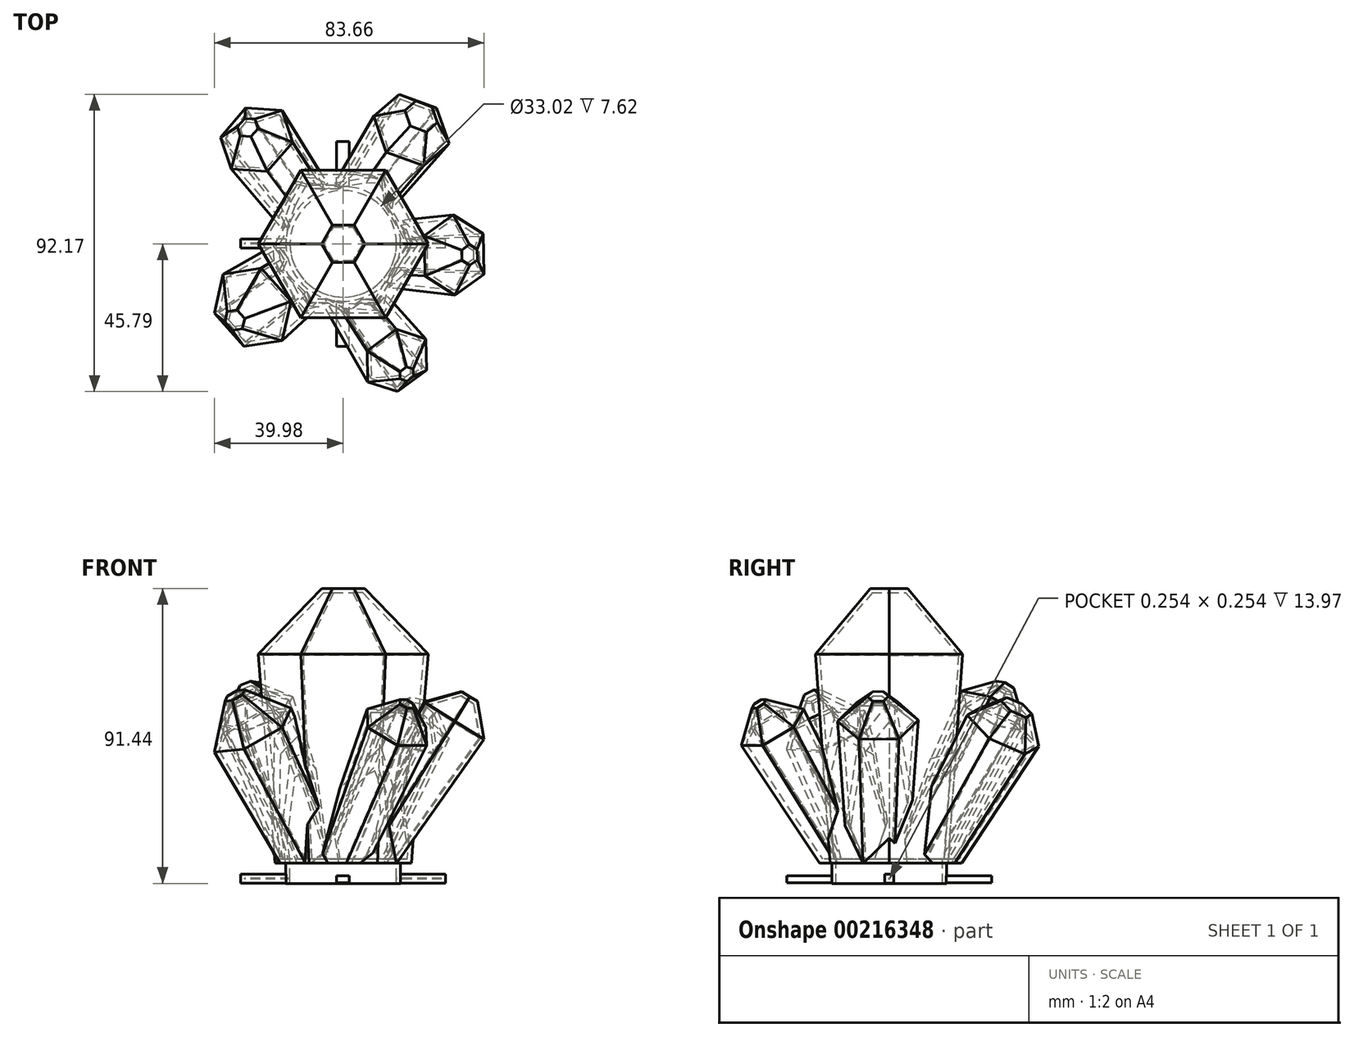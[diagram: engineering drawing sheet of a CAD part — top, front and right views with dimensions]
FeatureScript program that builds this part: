
annotation { "Feature Type Name" : "Feature", "Feature Type Description" : "" }
export const myFeature = defineFeature(function(context is Context, id is Id, definition is map)
    precondition{}
    {
        {
            var Q0;
            Q0=qCreatedBy(makeId("Top.planeOp"),FACE);
            cPlane(context, id + "F0", {"entities" : qUnion([Q0]), "cplaneType" : CPlaneType.OFFSET, "offset" : 35.56 * mm, "oppositeDirection" : true, "width" : 152.4 * mm, "height" : 152.4 * mm});
        }
        {
            var Q0;
            Q0=qCreatedBy(makeId("Top.planeOp"),FACE);
            var sketch = newSketch(context, id + "F1", { "sketchPlane" : qUnion([Q0])});
            skCircle(sketch, "E0.cCircle", {"center": v(0, 0) * mm, "radius": 38.1 * mm, "construction": true});
            skLineSegment(sketch, "E0.0", {"start": v(-12.38, 38.1) * mm, "end": v(12.38, 38.1) * mm});
            skLineSegment(sketch, "E0.1", {"start": v(12.38, 38.1) * mm, "end": v(32.4, 23.55) * mm});
            skLineSegment(sketch, "E0.2", {"start": v(32.4, 23.55) * mm, "end": v(40.06, 0) * mm});
            skLineSegment(sketch, "E0.3", {"start": v(40.06, 0) * mm, "end": v(32.4, -23.55) * mm});
            skLineSegment(sketch, "E0.4", {"start": v(32.4, -23.55) * mm, "end": v(12.38, -38.1) * mm});
            skLineSegment(sketch, "E0.5", {"start": v(12.38, -38.1) * mm, "end": v(-12.38, -38.1) * mm});
            skLineSegment(sketch, "E0.6", {"start": v(-12.38, -38.1) * mm, "end": v(-32.4, -23.55) * mm});
            skLineSegment(sketch, "E0.7", {"start": v(-32.4, -23.55) * mm, "end": v(-40.06, 0) * mm});
            skLineSegment(sketch, "E0.8", {"start": v(-40.06, 0) * mm, "end": v(-32.4, 23.55) * mm});
            skLineSegment(sketch, "E0.9", {"start": v(-32.4, 23.55) * mm, "end": v(-12.38, 38.1) * mm});
            skPoint(sketch, "E0.0.midPoint", {"position": v(0, 38.1) * mm});
            skSolve(sketch);
        }
        {
            var Q0;
            Q0=qCreatedBy(id+"F0.planeOp",FACE);
            var sketch = newSketch(context, id + "F2", { "sketchPlane" : qUnion([Q0])});
            skCircle(sketch, "E1.cCircle", {"center": v(0, 0) * mm, "radius": 19.05 * mm, "construction": true});
            skLineSegment(sketch, "E1.0", {"start": v(-6.19, 19.05) * mm, "end": v(6.19, 19.05) * mm});
            skLineSegment(sketch, "E1.1", {"start": v(6.19, 19.05) * mm, "end": v(16.2, 11.77) * mm});
            skLineSegment(sketch, "E1.2", {"start": v(16.2, 11.77) * mm, "end": v(20.03, 0) * mm});
            skLineSegment(sketch, "E1.3", {"start": v(20.03, 0) * mm, "end": v(16.2, -11.77) * mm});
            skLineSegment(sketch, "E1.4", {"start": v(16.2, -11.77) * mm, "end": v(6.19, -19.05) * mm});
            skLineSegment(sketch, "E1.5", {"start": v(6.19, -19.05) * mm, "end": v(-6.19, -19.05) * mm});
            skLineSegment(sketch, "E1.6", {"start": v(-6.19, -19.05) * mm, "end": v(-16.2, -11.77) * mm});
            skLineSegment(sketch, "E1.7", {"start": v(-16.2, -11.77) * mm, "end": v(-20.03, 0) * mm});
            skLineSegment(sketch, "E1.8", {"start": v(-20.03, 0) * mm, "end": v(-16.2, 11.77) * mm});
            skLineSegment(sketch, "E1.9", {"start": v(-16.2, 11.77) * mm, "end": v(-6.19, 19.05) * mm});
            skPoint(sketch, "E1.0.midPoint", {"position": v(0, 19.05) * mm});
            skSolve(sketch);
        }
        {
            var Q0;
            Q0=sQuery(id+"F1.wireOp",VERTEX,"E0.8.start");
            var Q1;
            Q1=sQuery(id+"F2.wireOp",VERTEX,"E1.2.start");
            var Q2;
            Q2=sQuery(id+"F2.wireOp",VERTEX,"E1.4.start");
            cPlane(context, id + "F3", {"entities" : qUnion([Q0, Q1, Q2]), "cplaneType" : CPlaneType.THREE_POINT, "offset" : 25.4 * mm, "width" : 152.4 * mm, "height" : 152.4 * mm});
        }
        {
            var Q0;
            Q0=sQuery(id+"F1.wireOp",VERTEX,"E0.6.start");
            var Q1;
            Q1=sQuery(id+"F2.wireOp",VERTEX,"E1.9.end");
            var Q2;
            Q2=sQuery(id+"F2.wireOp",VERTEX,"E1.3.start");
            cPlane(context, id + "F4", {"entities" : qUnion([Q0, Q1, Q2]), "cplaneType" : CPlaneType.THREE_POINT, "offset" : 25.4 * mm, "width" : 152.4 * mm, "height" : 152.4 * mm});
        }
        {
            var Q0;
            Q0=sQuery(id+"F1.wireOp",VERTEX,"E0.4.start");
            var Q1;
            Q1=sQuery(id+"F2.wireOp",VERTEX,"E1.9.end");
            var Q2;
            Q2=sQuery(id+"F2.wireOp",VERTEX,"E1.8.end");
            cPlane(context, id + "F5", {"entities" : qUnion([Q0, Q1, Q2]), "cplaneType" : CPlaneType.THREE_POINT, "offset" : 25.4 * mm, "width" : 152.4 * mm, "height" : 152.4 * mm});
        }
        {
            var Q0;
            Q0=sQuery(id+"F1.wireOp",VERTEX,"E0.2.start");
            var Q1;
            Q1=sQuery(id+"F2.wireOp",VERTEX,"E1.8.start");
            var Q2;
            Q2=sQuery(id+"F2.wireOp",VERTEX,"E1.6.start");
            cPlane(context, id + "F6", {"entities" : qUnion([Q0, Q1, Q2]), "cplaneType" : CPlaneType.THREE_POINT, "offset" : 25.4 * mm, "width" : 152.4 * mm, "height" : 152.4 * mm});
        }
        {
            var Q0;
            Q0=sQuery(id+"F1.wireOp",VERTEX,"E0.9.end");
            var Q1;
            Q1=sQuery(id+"F2.wireOp",VERTEX,"E1.6.start");
            var Q2;
            Q2=sQuery(id+"F2.wireOp",VERTEX,"E1.3.start");
            cPlane(context, id + "F7", {"entities" : qUnion([Q0, Q1, Q2]), "cplaneType" : CPlaneType.THREE_POINT, "offset" : 25.4 * mm, "width" : 152.4 * mm, "height" : 152.4 * mm});
        }
        {
            var Q0;
            Q0=qCreatedBy(id+"F0.planeOp",FACE);
            var sketch = newSketch(context, id + "F8", { "sketchPlane" : qUnion([Q0])});
            skCircle(sketch, "E2.cCircle", {"center": v(0, 0) * mm, "radius": 17.14 * mm, "construction": true});
            skLineSegment(sketch, "E2.0", {"start": v(-9.9, 17.14) * mm, "end": v(9.9, 17.14) * mm});
            skLineSegment(sketch, "E2.1", {"start": v(9.9, 17.15) * mm, "end": v(19.8, 0) * mm});
            skLineSegment(sketch, "E2.2", {"start": v(19.8, 0) * mm, "end": v(9.9, -17.14) * mm});
            skLineSegment(sketch, "E2.3", {"start": v(9.9, -17.15) * mm, "end": v(-9.9, -17.15) * mm});
            skLineSegment(sketch, "E2.4", {"start": v(-9.9, -17.15) * mm, "end": v(-19.8, 0) * mm});
            skLineSegment(sketch, "E2.5", {"start": v(-19.8, 0) * mm, "end": v(-9.9, 17.15) * mm});
            skPoint(sketch, "E2.0.midPoint", {"position": v(0, 17.14) * mm});
            skSolve(sketch);
        }
        {
            var Q0;
            Q0 = qSketchRegion(id + "F8", true);
            extrude(context, id + "F9", {"entities" : qUnion([Q0]), "depth" : 81.28 * mm, "hasDraft" : true, "draftAngle" : 4 * degree});
        }
        {
            var Q0;
            Q0=makeQuery(id+"F9.opExtrude","CAP_FACE",FACE,{"disambiguationData":[OSD([sQuery(id+"F8.wireOp",EDGE,"E2.0"),sQuery(id+"F8.wireOp",EDGE,"E2.1"),sQuery(id+"F8.wireOp",EDGE,"E2.2"),sQuery(id+"F8.wireOp",EDGE,"E2.3"),sQuery(id+"F8.wireOp",EDGE,"E2.4"),sQuery(id+"F8.wireOp",EDGE,"E2.5")])],"isStart":false});
            var sketch = newSketch(context, id + "F10", { "sketchPlane" : qUnion([Q0])});
            skCircle(sketch, "E3.cCircle", {"center": v(0, 0) * mm, "radius": 22.83 * mm, "construction": true});
            skLineSegment(sketch, "E3.0", {"start": v(-13.18, 22.83) * mm, "end": v(13.18, 22.83) * mm});
            skLineSegment(sketch, "E3.1", {"start": v(13.18, 22.83) * mm, "end": v(26.36, 0) * mm});
            skLineSegment(sketch, "E3.2", {"start": v(26.36, 0) * mm, "end": v(13.18, -22.83) * mm});
            skLineSegment(sketch, "E3.3", {"start": v(13.18, -22.83) * mm, "end": v(-13.18, -22.83) * mm});
            skLineSegment(sketch, "E3.4", {"start": v(-13.18, -22.83) * mm, "end": v(-26.36, 0) * mm});
            skLineSegment(sketch, "E3.5", {"start": v(-26.36, 0) * mm, "end": v(-13.18, 22.83) * mm});
            skPoint(sketch, "E3.0.midPoint", {"position": v(0, 22.83) * mm});
            skSolve(sketch);
        }
        {
            var Q0;
            Q0 = qSketchRegion(id + "F10", true);
            extrude(context, id + "F11", {"entities" : qUnion([Q0]), "operationType" : NewBodyOperationType.ADD, "depth" : 20.32 * mm, "hasDraft" : true, "draftAngle" : 40 * degree, "draftPullDirection" : true});
        }
        {
            var Q0;
            Q0=qCreatedBy(id+"F3.planeOp",FACE);
            var sketch = newSketch(context, id + "F12", { "sketchPlane" : qUnion([Q0])});
            skCircle(sketch, "E4.cCircle", {"center": v(15.7, -3.44) * mm, "radius": 7.62 * mm, "construction": true});
            skLineSegment(sketch, "E4.0", {"start": v(7.97, 0.77) * mm, "end": v(15.47, 5.36) * mm});
            skLineSegment(sketch, "E4.1", {"start": v(15.47, 5.36) * mm, "end": v(23.2, 1.15) * mm});
            skLineSegment(sketch, "E4.2", {"start": v(23.2, 1.15) * mm, "end": v(23.43, -7.64) * mm});
            skLineSegment(sketch, "E4.3", {"start": v(23.43, -7.64) * mm, "end": v(15.92, -12.23) * mm});
            skLineSegment(sketch, "E4.4", {"start": v(15.92, -12.23) * mm, "end": v(8.2, -8.03) * mm});
            skLineSegment(sketch, "E4.5", {"start": v(8.2, -8.03) * mm, "end": v(7.97, 0.77) * mm});
            skPoint(sketch, "E4.0.midPoint", {"position": v(11.72, 3.06) * mm});
            skSolve(sketch);
        }
        {
            var Q0;
            Q0 = qSketchRegion(id + "F12", true);
            extrude(context, id + "F13", {"entities" : qUnion([Q0]), "operationType" : NewBodyOperationType.ADD, "depth" : 60.96 * mm, "hasDraft" : true, "draftAngle" : 3 * degree});
        }
        {
            var Q0;
            Q0=makeQuery(id+"F13.opExtrude","CAP_FACE",FACE,{"disambiguationData":[OSD([sQuery(id+"F12.wireOp",EDGE,"E4.0"),sQuery(id+"F12.wireOp",EDGE,"E4.1"),sQuery(id+"F12.wireOp",EDGE,"E4.2"),sQuery(id+"F12.wireOp",EDGE,"E4.3"),sQuery(id+"F12.wireOp",EDGE,"E4.4"),sQuery(id+"F12.wireOp",EDGE,"E4.5")])],"isStart":false});
            var sketch = newSketch(context, id + "F14", { "sketchPlane" : qUnion([Q0])});
            skLineSegment(sketch, "E5", {"start": v(4.73, 2.53) * mm, "end": v(26.67, -9.4) * mm, "construction": true});
            skPoint(sketch, "E6", {"position": v(15.7, -3.44) * mm});
            skCircle(sketch, "E7.cCircle", {"center": v(15.7, -3.44) * mm, "radius": 10.81 * mm, "construction": true});
            skLineSegment(sketch, "E7.0", {"start": v(15.38, 9.05) * mm, "end": v(26.35, 3.08) * mm});
            skLineSegment(sketch, "E7.1", {"start": v(26.35, 3.08) * mm, "end": v(26.67, -9.4) * mm});
            skLineSegment(sketch, "E7.2", {"start": v(26.67, -9.4) * mm, "end": v(16.01, -15.92) * mm});
            skLineSegment(sketch, "E7.3", {"start": v(16.01, -15.92) * mm, "end": v(5.04, -9.95) * mm});
            skLineSegment(sketch, "E7.4", {"start": v(5.04, -9.95) * mm, "end": v(4.73, 2.53) * mm});
            skLineSegment(sketch, "E7.5", {"start": v(4.73, 2.53) * mm, "end": v(15.38, 9.05) * mm});
            skPoint(sketch, "E7.0.midPoint", {"position": v(20.86, 6.06) * mm});
            skSolve(sketch);
        }
        {
            var Q0;
            Q0 = qSketchRegion(id + "F14", true);
            extrude(context, id + "F15", {"entities" : qUnion([Q0]), "operationType" : NewBodyOperationType.ADD, "depth" : 8.9 * mm, "hasDraft" : true, "draftAngle" : 42 * degree, "draftPullDirection" : true});
        }
        {
            var Q0;
            Q0=qCreatedBy(id+"F4.planeOp",FACE);
            var sketch = newSketch(context, id + "F16", { "sketchPlane" : qUnion([Q0])});
            skCircle(sketch, "E8.cCircle", {"center": v(7.36, 19.64) * mm, "radius": 7.62 * mm, "construction": true});
            skLineSegment(sketch, "E8.0", {"start": v(13.16, 26.26) * mm, "end": v(16, 17.93) * mm});
            skLineSegment(sketch, "E8.1", {"start": v(16, 17.93) * mm, "end": v(10.2, 11.3) * mm});
            skLineSegment(sketch, "E8.2", {"start": v(10.2, 11.3) * mm, "end": v(1.57, 13.01) * mm});
            skLineSegment(sketch, "E8.3", {"start": v(1.57, 13.01) * mm, "end": v(-1.27, 21.34) * mm});
            skLineSegment(sketch, "E8.4", {"start": v(-1.27, 21.34) * mm, "end": v(4.53, 27.96) * mm});
            skLineSegment(sketch, "E8.5", {"start": v(4.53, 27.96) * mm, "end": v(13.16, 26.26) * mm});
            skPoint(sketch, "E8.0.midPoint", {"position": v(14.58, 22.1) * mm});
            skSolve(sketch);
        }
        {
            var Q0;
            Q0 = qSketchRegion(id + "F16", true);
            extrude(context, id + "F17", {"entities" : qUnion([Q0]), "operationType" : NewBodyOperationType.ADD, "depth" : 63.75 * mm, "hasDraft" : true, "draftAngle" : 3 * degree});
        }
        {
            var Q0;
            Q0=makeQuery(id+"F17.opExtrude","CAP_FACE",FACE,{"disambiguationData":[OSD([sQuery(id+"F16.wireOp",EDGE,"E8.0"),sQuery(id+"F16.wireOp",EDGE,"E8.1"),sQuery(id+"F16.wireOp",EDGE,"E8.2"),sQuery(id+"F16.wireOp",EDGE,"E8.3"),sQuery(id+"F16.wireOp",EDGE,"E8.4"),sQuery(id+"F16.wireOp",EDGE,"E8.5")])],"isStart":false});
            var sketch = newSketch(context, id + "F18", { "sketchPlane" : qUnion([Q0])});
            skLineSegment(sketch, "E9", {"start": v(19.78, 17.18) * mm, "end": v(-5.05, 22.1) * mm, "construction": true});
            skCircle(sketch, "E10.cCircle", {"center": v(7.36, 19.64) * mm, "radius": 10.96 * mm, "construction": true});
            skLineSegment(sketch, "E10.0", {"start": v(11.45, 7.65) * mm, "end": v(-0.97, 10.11) * mm});
            skLineSegment(sketch, "E10.1", {"start": v(-0.97, 10.11) * mm, "end": v(-5.05, 22.1) * mm});
            skLineSegment(sketch, "E10.2", {"start": v(-5.05, 22.1) * mm, "end": v(3.28, 31.62) * mm});
            skLineSegment(sketch, "E10.3", {"start": v(3.28, 31.62) * mm, "end": v(15.7, 29.16) * mm});
            skLineSegment(sketch, "E10.4", {"start": v(15.7, 29.16) * mm, "end": v(19.78, 17.18) * mm});
            skLineSegment(sketch, "E10.5", {"start": v(19.78, 17.18) * mm, "end": v(11.45, 7.65) * mm});
            skPoint(sketch, "E10.0.midPoint", {"position": v(5.24, 8.88) * mm});
            skSolve(sketch);
        }
        {
            var Q0;
            Q0 = qSketchRegion(id + "F18", true);
            extrude(context, id + "F19", {"entities" : qUnion([Q0]), "operationType" : NewBodyOperationType.ADD, "depth" : 8.9 * mm, "hasDraft" : true, "draftAngle" : 35 * degree, "draftPullDirection" : true});
        }
        {
            var Q0;
            Q0=qCreatedBy(id+"F5.planeOp",FACE);
            var sketch = newSketch(context, id + "F20", { "sketchPlane" : qUnion([Q0])});
            skCircle(sketch, "E11.cCircle", {"center": v(-13.26, -16.2) * mm, "radius": 8.17 * mm, "construction": true});
            skLineSegment(sketch, "E11.0", {"start": v(-22.46, -18.32) * mm, "end": v(-19.69, -9.3) * mm});
            skLineSegment(sketch, "E11.1", {"start": v(-19.69, -9.3) * mm, "end": v(-10.49, -7.19) * mm});
            skLineSegment(sketch, "E11.2", {"start": v(-10.49, -7.19) * mm, "end": v(-4.06, -14.1) * mm});
            skLineSegment(sketch, "E11.3", {"start": v(-4.06, -14.1) * mm, "end": v(-6.82, -23.12) * mm});
            skLineSegment(sketch, "E11.4", {"start": v(-6.82, -23.12) * mm, "end": v(-16.02, -25.23) * mm});
            skLineSegment(sketch, "E11.5", {"start": v(-16.02, -25.23) * mm, "end": v(-22.46, -18.32) * mm});
            skPoint(sketch, "E11.0.midPoint", {"position": v(-21.07, -13.81) * mm});
            skSolve(sketch);
        }
        {
            var Q0;
            Q0 = qSketchRegion(id + "F20", true);
            extrude(context, id + "F21", {"entities" : qUnion([Q0]), "operationType" : NewBodyOperationType.ADD, "oppositeDirection" : true, "depth" : 66.04 * mm, "hasDraft" : true, "draftAngle" : 2 * degree});
        }
        {
            var Q0;
            Q0=makeQuery(id+"F21.opExtrude","CAP_FACE",FACE,{"disambiguationData":[OSD([sQuery(id+"F20.wireOp",EDGE,"E11.0"),sQuery(id+"F20.wireOp",EDGE,"E11.1"),sQuery(id+"F20.wireOp",EDGE,"E11.2"),sQuery(id+"F20.wireOp",EDGE,"E11.3"),sQuery(id+"F20.wireOp",EDGE,"E11.4"),sQuery(id+"F20.wireOp",EDGE,"E11.5")])],"isStart":false});
            var sketch = newSketch(context, id + "F22", { "sketchPlane" : qUnion([Q0])});
            skLineSegment(sketch, "E12", {"start": v(-21.5, 7.35) * mm, "end": v(-5.01, 25.07) * mm, "construction": true});
            skCircle(sketch, "E13.cCircle", {"center": v(-13.26, 16.2) * mm, "radius": 10.48 * mm, "construction": true});
            skLineSegment(sketch, "E13.0", {"start": v(-25.05, 18.92) * mm, "end": v(-16.8, 27.78) * mm});
            skLineSegment(sketch, "E13.1", {"start": v(-16.8, 27.78) * mm, "end": v(-5.01, 25.07) * mm});
            skLineSegment(sketch, "E13.2", {"start": v(-5.01, 25.07) * mm, "end": v(-1.46, 13.5) * mm});
            skLineSegment(sketch, "E13.3", {"start": v(-1.46, 13.5) * mm, "end": v(-9.7, 4.64) * mm});
            skLineSegment(sketch, "E13.4", {"start": v(-9.7, 4.64) * mm, "end": v(-21.5, 7.35) * mm});
            skLineSegment(sketch, "E13.5", {"start": v(-21.5, 7.35) * mm, "end": v(-25.05, 18.92) * mm});
            skPoint(sketch, "E13.0.midPoint", {"position": v(-20.93, 23.35) * mm});
            skSolve(sketch);
        }
        {
            var Q0;
            Q0 = qSketchRegion(id + "F22", true);
            extrude(context, id + "F23", {"entities" : qUnion([Q0]), "operationType" : NewBodyOperationType.ADD, "depth" : 8.9 * mm, "hasDraft" : true, "draftAngle" : 40 * degree, "draftPullDirection" : true});
        }
        {
            var Q0;
            Q0=qCreatedBy(id+"F6.planeOp",FACE);
            var sketch = newSketch(context, id + "F24", { "sketchPlane" : qUnion([Q0])});
            skCircle(sketch, "E14.cCircle", {"center": v(-13.43, 10.73) * mm, "radius": 8.9 * mm, "construction": true});
            skLineSegment(sketch, "E14.0", {"start": v(-20.98, 3.78) * mm, "end": v(-23.22, 13.8) * mm});
            skLineSegment(sketch, "E14.1", {"start": v(-23.22, 13.8) * mm, "end": v(-15.67, 20.75) * mm});
            skLineSegment(sketch, "E14.2", {"start": v(-15.67, 20.75) * mm, "end": v(-5.87, 17.68) * mm});
            skLineSegment(sketch, "E14.3", {"start": v(-5.87, 17.68) * mm, "end": v(-3.63, 7.67) * mm});
            skLineSegment(sketch, "E14.4", {"start": v(-3.63, 7.67) * mm, "end": v(-11.18, 0.72) * mm});
            skLineSegment(sketch, "E14.5", {"start": v(-11.18, 0.72) * mm, "end": v(-20.98, 3.78) * mm});
            skPoint(sketch, "E14.0.midPoint", {"position": v(-22.1, 8.79) * mm});
            skSolve(sketch);
        }
        {
            var Q0;
            Q0 = qSketchRegion(id + "F24", true);
            extrude(context, id + "F25", {"entities" : qUnion([Q0]), "operationType" : NewBodyOperationType.ADD, "oppositeDirection" : true, "depth" : 58.42 * mm, "hasDraft" : true, "draftAngle" : 3 * degree});
        }
        {
            var Q0;
            Q0=makeQuery(id+"F25.opExtrude","CAP_FACE",FACE,{"disambiguationData":[OSD([sQuery(id+"F24.wireOp",EDGE,"E14.0"),sQuery(id+"F24.wireOp",EDGE,"E14.1"),sQuery(id+"F24.wireOp",EDGE,"E14.2"),sQuery(id+"F24.wireOp",EDGE,"E14.3"),sQuery(id+"F24.wireOp",EDGE,"E14.4"),sQuery(id+"F24.wireOp",EDGE,"E14.5")])],"isStart":false});
            var sketch = newSketch(context, id + "F26", { "sketchPlane" : qUnion([Q0])});
            skLineSegment(sketch, "E15", {"start": v(-26.6, -14.85) * mm, "end": v(-0.26, -6.61) * mm, "construction": true});
            skCircle(sketch, "E16.cCircle", {"center": v(-13.43, -10.73) * mm, "radius": 11.95 * mm, "construction": true});
            skLineSegment(sketch, "E16.0", {"start": v(-23.58, -1.39) * mm, "end": v(-10.4, 2.73) * mm});
            skLineSegment(sketch, "E16.1", {"start": v(-10.4, 2.73) * mm, "end": v(-0.26, -6.61) * mm});
            skLineSegment(sketch, "E16.2", {"start": v(-0.26, -6.61) * mm, "end": v(-3.27, -20.08) * mm});
            skLineSegment(sketch, "E16.3", {"start": v(-3.27, -20.08) * mm, "end": v(-16.44, -24.2) * mm});
            skLineSegment(sketch, "E16.4", {"start": v(-16.44, -24.2) * mm, "end": v(-26.6, -14.85) * mm});
            skLineSegment(sketch, "E16.5", {"start": v(-26.6, -14.85) * mm, "end": v(-23.58, -1.39) * mm});
            skPoint(sketch, "E16.0.midPoint", {"position": v(-17, 0.67) * mm});
            skSolve(sketch);
        }
        {
            var Q0;
            Q0 = qSketchRegion(id + "F26", true);
            extrude(context, id + "F27", {"entities" : qUnion([Q0]), "operationType" : NewBodyOperationType.ADD, "depth" : 12.7 * mm, "hasDraft" : true, "draftAngle" : 35 * degree, "draftPullDirection" : true});
        }
        {
            var Q0;
            Q0=qCreatedBy(id+"F7.planeOp",FACE);
            var sketch = newSketch(context, id + "F28", { "sketchPlane" : qUnion([Q0])});
            skCircle(sketch, "E17.cCircle", {"center": v(2.67, 19.82) * mm, "radius": 6.35 * mm, "construction": true});
            skLineSegment(sketch, "E17.0", {"start": v(8.95, 16.04) * mm, "end": v(2.53, 12.5) * mm});
            skLineSegment(sketch, "E17.1", {"start": v(2.53, 12.5) * mm, "end": v(-3.75, 16.27) * mm});
            skLineSegment(sketch, "E17.2", {"start": v(-3.75, 16.27) * mm, "end": v(-3.61, 23.6) * mm});
            skLineSegment(sketch, "E17.3", {"start": v(-3.61, 23.6) * mm, "end": v(2.8, 27.15) * mm});
            skLineSegment(sketch, "E17.4", {"start": v(2.8, 27.15) * mm, "end": v(9.09, 23.37) * mm});
            skLineSegment(sketch, "E17.5", {"start": v(9.09, 23.37) * mm, "end": v(8.95, 16.04) * mm});
            skPoint(sketch, "E17.0.midPoint", {"position": v(5.74, 14.27) * mm});
            skSolve(sketch);
        }
        {
            var Q0;
            Q0 = qSketchRegion(id + "F28", true);
            extrude(context, id + "F29", {"entities" : qUnion([Q0]), "operationType" : NewBodyOperationType.ADD, "oppositeDirection" : true, "depth" : 63.5 * mm, "hasDraft" : true, "draftAngle" : 3 * degree});
        }
        {
            var Q0;
            Q0=makeQuery(id+"F29.opExtrude","CAP_FACE",FACE,{"disambiguationData":[OSD([sQuery(id+"F28.wireOp",EDGE,"E17.0"),sQuery(id+"F28.wireOp",EDGE,"E17.1"),sQuery(id+"F28.wireOp",EDGE,"E17.2"),sQuery(id+"F28.wireOp",EDGE,"E17.3"),sQuery(id+"F28.wireOp",EDGE,"E17.4"),sQuery(id+"F28.wireOp",EDGE,"E17.5")])],"isStart":false});
            var sketch = newSketch(context, id + "F30", { "sketchPlane" : qUnion([Q0])});
            skLineSegment(sketch, "E18", {"start": v(-6.9, -25.59) * mm, "end": v(12.24, -14.06) * mm, "construction": true});
            skCircle(sketch, "E19.cCircle", {"center": v(2.67, -19.82) * mm, "radius": 9.68 * mm, "construction": true});
            skLineSegment(sketch, "E19.0", {"start": v(-7.1, -14.41) * mm, "end": v(2.46, -8.65) * mm});
            skLineSegment(sketch, "E19.1", {"start": v(2.46, -8.65) * mm, "end": v(12.24, -14.06) * mm});
            skLineSegment(sketch, "E19.2", {"start": v(12.24, -14.06) * mm, "end": v(12.45, -25.23) * mm});
            skLineSegment(sketch, "E19.3", {"start": v(12.45, -25.23) * mm, "end": v(2.88, -31) * mm});
            skLineSegment(sketch, "E19.4", {"start": v(2.88, -31) * mm, "end": v(-6.9, -25.59) * mm});
            skLineSegment(sketch, "E19.5", {"start": v(-6.9, -25.59) * mm, "end": v(-7.1, -14.41) * mm});
            skPoint(sketch, "E19.0.midPoint", {"position": v(-2.32, -11.53) * mm});
            skSolve(sketch);
        }
        {
            var Q0;
            Q0 = qSketchRegion(id + "F30", true);
            extrude(context, id + "F31", {"entities" : qUnion([Q0]), "operationType" : NewBodyOperationType.ADD, "depth" : 8.9 * mm, "hasDraft" : true, "draftAngle" : 40 * degree, "draftPullDirection" : true});
        }
        {
            var Q0;
            Q0=qCreatedBy(makeId("Top.planeOp"),FACE);
            cPlane(context, id + "F32", {"entities" : qUnion([Q0]), "cplaneType" : CPlaneType.OFFSET, "offset" : 19.05 * mm, "oppositeDirection" : true, "width" : 152.4 * mm, "height" : 152.4 * mm});
        }
        {
            var Q0;
            Q0=qCreatedBy(id+"F32.planeOp",FACE);
            var sketch = newSketch(context, id + "F33", { "sketchPlane" : qUnion([Q0])});
            skLineSegment(sketch, "E20.bottom", {"start": v(-40.64, 40.64) * mm, "end": v(40.64, 40.64) * mm, "construction": true});
            skLineSegment(sketch, "E20.top", {"start": v(-40.64, -40.64) * mm, "end": v(40.64, -40.64) * mm, "construction": true});
            skLineSegment(sketch, "E20.left", {"start": v(-40.64, 40.64) * mm, "end": v(-40.64, -40.64) * mm, "construction": true});
            skLineSegment(sketch, "E20.right", {"start": v(40.64, 40.64) * mm, "end": v(40.64, -40.64) * mm, "construction": true});
            skLineSegment(sketch, "E21", {"start": v(-40.64, 0) * mm, "end": v(40.64, 0) * mm, "construction": true});
            skLineSegment(sketch, "E22", {"start": v(0, 40.64) * mm, "end": v(0, -40.64) * mm, "construction": true});
            skCircle(sketch, "E23", {"center": v(0, 0) * mm, "radius": 40.64 * mm});
            skSolve(sketch);
        }
        {
            var Q0;
            Q0 = qSketchRegion(id + "F33", true);
            extrude(context, id + "F34", {"entities" : qUnion([Q0]), "operationType" : NewBodyOperationType.REMOVE, "oppositeDirection" : true, "depth" : 25.4 * mm});
        }
        {
            var Q0;
            Q0=makeQuery(id+"F34.boolean.opBoolean","COPY",FACE,{"derivedFrom":makeQuery(id+"F34.opExtrude","CAP_FACE",FACE,{"disambiguationData":[OSD([sQuery(id+"F33.wireOp",EDGE,"E23")])],"isStart":true})});
            var sketch = newSketch(context, id + "F35", { "sketchPlane" : qUnion([Q0])});
            skCircle(sketch, "E24", {"center": v(0, 0) * mm, "radius": 17.78 * mm});
            skSolve(sketch);
        }
        {
            var Q0;
            Q0 = qSketchRegion(id + "F35", true);
            extrude(context, id + "F36", {"entities" : qUnion([Q0]), "operationType" : NewBodyOperationType.ADD, "depth" : 6.35 * mm});
        }
        {
            var Q0;
            Q0=qCreatedBy(makeId("Front.planeOp"),FACE);
            var sketch = newSketch(context, id + "F37", { "sketchPlane" : qUnion([Q0])});
            skLineSegment(sketch, "E25.bottom", {"start": v(-2.03, -25.25) * mm, "end": v(1.9, -25.25) * mm});
            skLineSegment(sketch, "E25.top", {"start": v(-2.03, -23.1) * mm, "end": v(1.9, -23.1) * mm});
            skLineSegment(sketch, "E25.left", {"start": v(-2.03, -25.25) * mm, "end": v(-2.03, -23.1) * mm});
            skLineSegment(sketch, "E25.right", {"start": v(1.9, -25.25) * mm, "end": v(1.9, -23.1) * mm});
            skPoint(sketch, "E26", {"position": v(-0.07, -23.1) * mm});
            skSolve(sketch);
        }
        {
            var Q0;
            Q0 = qSketchRegion(id + "F37", true);
            extrude(context, id + "F38", {"entities" : qUnion([Q0]), "operationType" : NewBodyOperationType.ADD, "depth" : 31.75 * mm, "hasSecondDirection" : true, "secondDirectionOppositeDirection" : true, "secondDirectionDepth" : 31.75 * mm});
        }
        {
            var Q0;
            Q0=qCreatedBy(makeId("Right.planeOp"),FACE);
            var sketch = newSketch(context, id + "F39", { "sketchPlane" : qUnion([Q0])});
            skLineSegment(sketch, "E27.bottom", {"start": v(-1.3, -25.28) * mm, "end": v(1.5, -25.28) * mm});
            skLineSegment(sketch, "E27.top", {"start": v(-1.3, -22.49) * mm, "end": v(1.5, -22.49) * mm});
            skLineSegment(sketch, "E27.left", {"start": v(-1.3, -25.28) * mm, "end": v(-1.3, -22.49) * mm});
            skLineSegment(sketch, "E27.right", {"start": v(1.5, -25.28) * mm, "end": v(1.5, -22.49) * mm});
            skPoint(sketch, "E28", {"position": v(0.1, -22.49) * mm});
            skSolve(sketch);
        }
        {
            var Q0;
            Q0 = qSketchRegion(id + "F39", true);
            extrude(context, id + "F40", {"entities" : qUnion([Q0]), "operationType" : NewBodyOperationType.ADD, "depth" : 31.75 * mm, "hasSecondDirection" : true, "secondDirectionOppositeDirection" : true, "secondDirectionDepth" : 31.75 * mm});
        }
        {
            var Q0;
            Q0=makeQuery(id+"F36.opExtrude","CAP_FACE",FACE,{"disambiguationData":[OSD([sQuery(id+"F35.wireOp",EDGE,"E24")])],"isStart":false});
            shell(context, id + "F41", {"entities" : qUnion([Q0]), "thickness" : 1.27 * mm});
        }
    });
